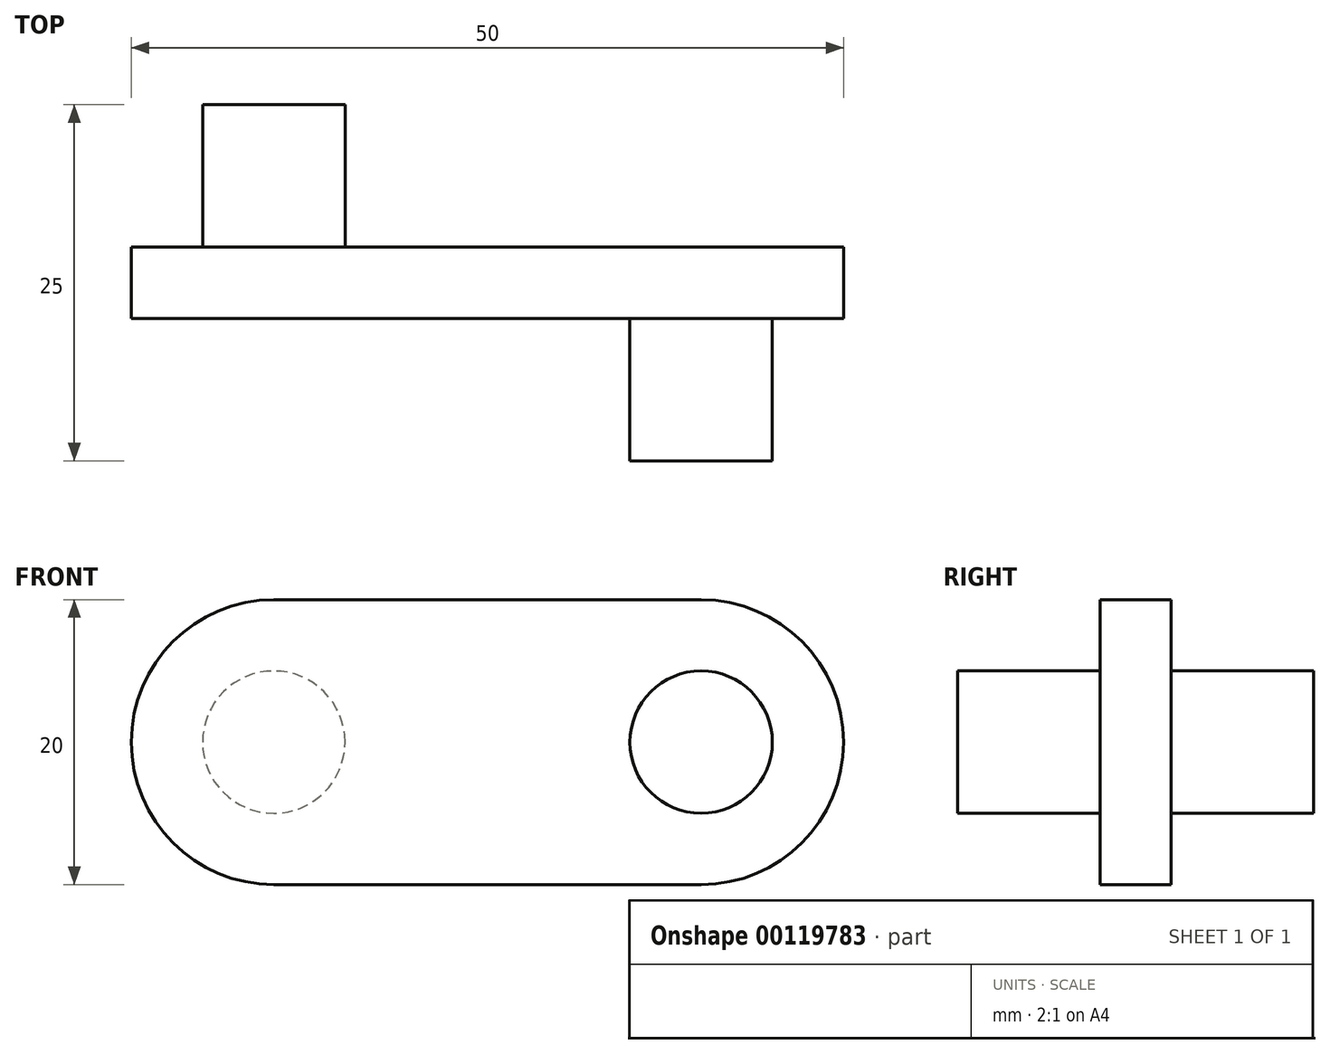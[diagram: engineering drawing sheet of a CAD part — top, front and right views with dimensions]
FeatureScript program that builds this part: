
annotation { "Feature Type Name" : "Feature", "Feature Type Description" : "" }
export const myFeature = defineFeature(function(context is Context, id is Id, definition is map)
    precondition{}
    {
        {
            var Q0;
            Q0=qCreatedBy(makeId("Front.planeOp"),FACE);
            var sketch = newSketch(context, id + "F0", { "sketchPlane" : qUnion([Q0])});
            skLineSegment(sketch, "E0", {"start": v(0, 0) * mm, "end": v(30, 0) * mm});
            skLineSegment(sketch, "E1", {"start": v(0, 20) * mm, "end": v(30, 20) * mm});
            skArc(sketch, "E2", {"start": v(0, 20) * mm, "mid": v(-10, 10) * mm, "end": v(0, 0) * mm});
            skArc(sketch, "E3", {"start": v(30, 0) * mm, "mid": v(40, 10) * mm, "end": v(30, 20) * mm});
            skSolve(sketch);
        }
        {
            var Q0;
            Q0 = qSketchRegion(id + "F0", true);
            extrude(context, id + "F1", {"entities" : qUnion([Q0]), "endBound" : BoundingType.SYMMETRIC, "depth" : 5 * mm});
        }
        {
            var Q0;
            Q0=makeQuery(id+"F1.opExtrude","CAP_FACE",FACE,{"disambiguationData":[OSD([sQuery(id+"F0.wireOp",EDGE,"E0"),sQuery(id+"F0.wireOp",EDGE,"E1"),sQuery(id+"F0.wireOp",EDGE,"E2"),sQuery(id+"F0.wireOp",EDGE,"E3")])],"isStart":false});
            var sketch = newSketch(context, id + "F2", { "sketchPlane" : qUnion([Q0])});
            skCircle(sketch, "E4", {"center": v(30, 10) * mm, "radius": 5 * mm});
            skSolve(sketch);
        }
        {
            var Q0;
            Q0 = qSketchRegion(id + "F2", true);
            extrude(context, id + "F3", {"entities" : qUnion([Q0]), "operationType" : NewBodyOperationType.ADD, "depth" : 10 * mm});
        }
        {
            var Q0;
            Q0=makeQuery(id+"F1.opExtrude","CAP_FACE",FACE,{"disambiguationData":[OSD([sQuery(id+"F0.wireOp",EDGE,"E0"),sQuery(id+"F0.wireOp",EDGE,"E1"),sQuery(id+"F0.wireOp",EDGE,"E2"),sQuery(id+"F0.wireOp",EDGE,"E3")])],"isStart":true});
            var sketch = newSketch(context, id + "F4", { "sketchPlane" : qUnion([Q0])});
            skCircle(sketch, "E5", {"center": v(0, 10) * mm, "radius": 5 * mm});
            skSolve(sketch);
        }
        {
            var Q0;
            Q0 = qSketchRegion(id + "F4", true);
            extrude(context, id + "F5", {"entities" : qUnion([Q0]), "operationType" : NewBodyOperationType.ADD, "depth" : 10 * mm});
        }
    });
